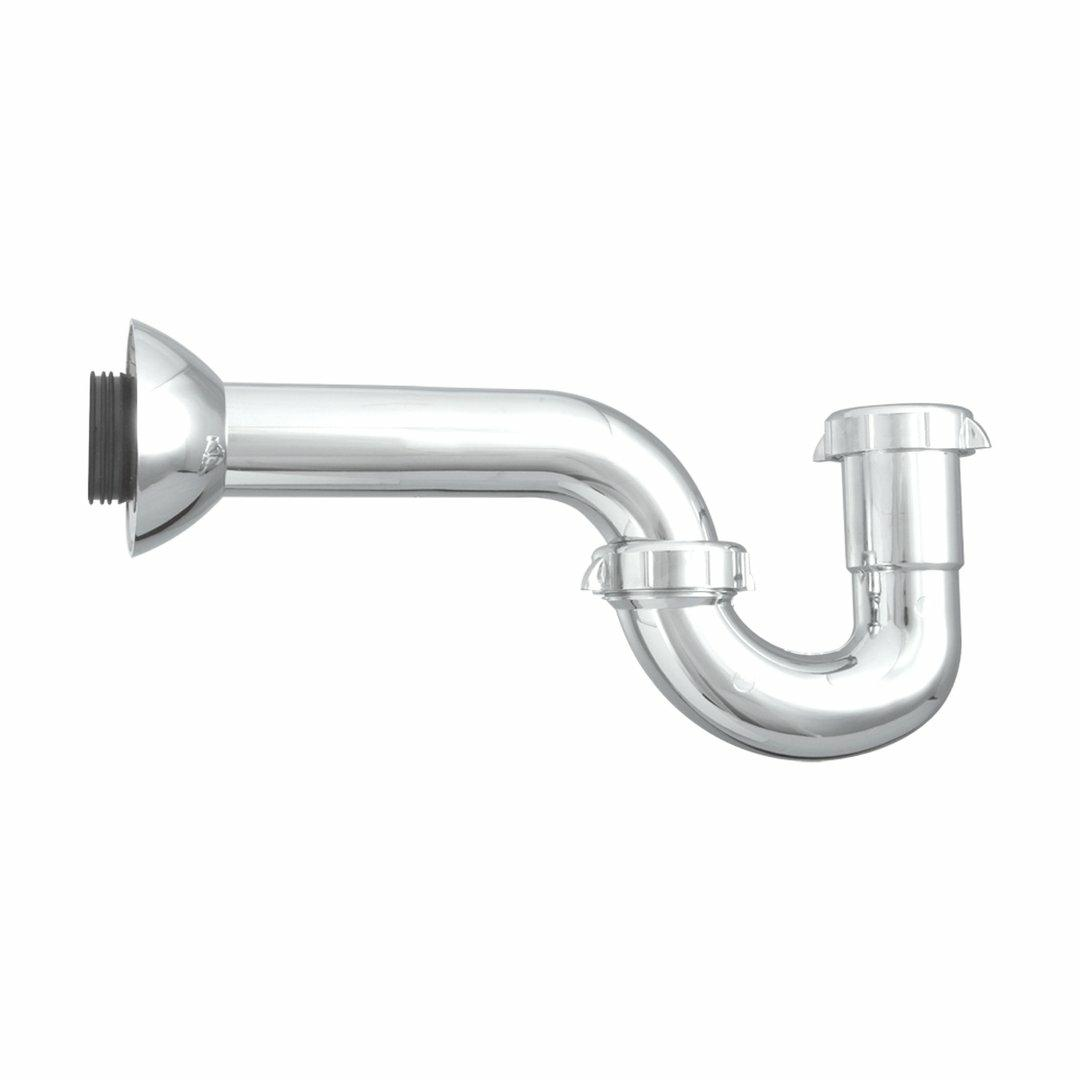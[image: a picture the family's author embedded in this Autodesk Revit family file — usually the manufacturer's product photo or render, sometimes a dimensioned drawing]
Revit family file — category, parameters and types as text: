
# Revit family: 01-2053-15 LAVAMANOS VESSEL DALY II
name_source: partatom
category: Plumbing Fixtures
revit_build: Autodesk Revit 2018 (Build: 20170223_1515(x64)
units: mm (PartAtom-declared; Revit-internal decimal feet)

## family parameters
Cut with Voids When Loaded = No
Host = Face
OmniClass Number = 23.31.11.00
Part Type = Normal
Room Calculation Point = No
Round Connector Dimension = Use Diameter
Shared = No

## types (1)
- 01-2053-15
    Alto = 135 mm  [stored 0.442913 ft]
    CW Connection = Yes
    Ceramica = Porcelana
    Default Elevation = 0 mm  [stored 0 ft]
    Description = Lavamanos tipo vessel redondo
    Diametro = 360 mm
    HW Connection = Yes
    Link Ficha Tecnica = http://infotecnica.gricol.com
    Manufacturer = Gricol
    Model = 01-2053-15
    Product Name = LAVAMANOS VESSEL DALY II
    Push = push cromado
    Type Image = LAVAMANOS Dally II FOTO.jpg
    URL = https://www.gricol.com
    Vent Connection = No
    Waste Connection = No

note: [stored X ft] marks values corroborated as IEEE doubles in the binary element streams (Revit-internal decimal feet)

## geometry (parser evidence)
native form markers: Blend x8, Sweep x11
no freeform markers — native parametric forms only
